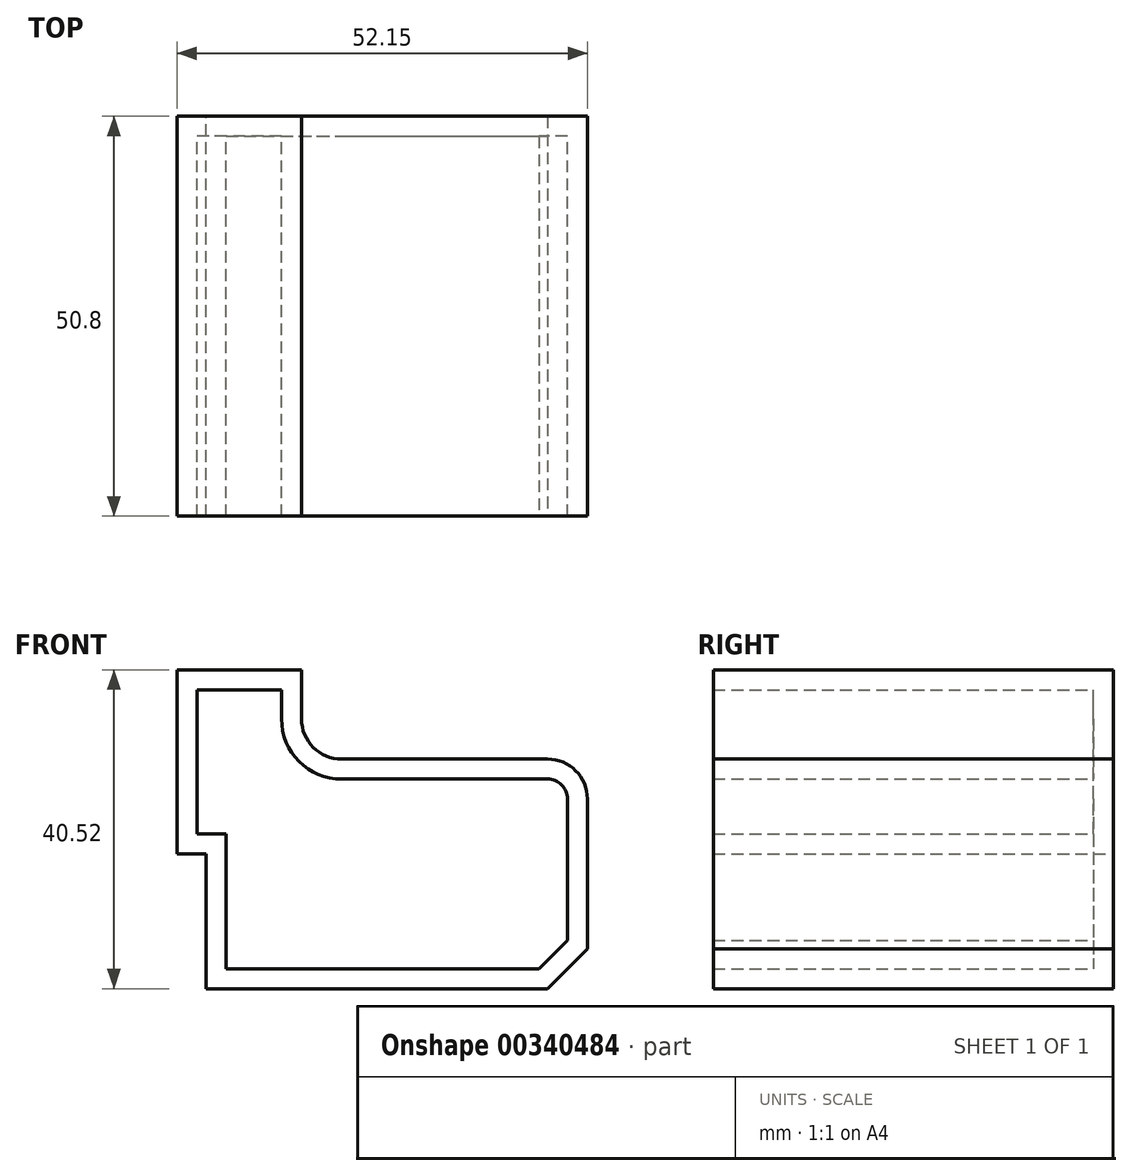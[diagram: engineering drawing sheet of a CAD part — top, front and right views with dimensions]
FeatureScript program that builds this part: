
annotation { "Feature Type Name" : "Feature", "Feature Type Description" : "" }
export const myFeature = defineFeature(function(context is Context, id is Id, definition is map)
    precondition{}
    {
        {
            var Q0;
            Q0=qCreatedBy(makeId("Front.planeOp"),FACE);
            var sketch = newSketch(context, id + "F0", { "sketchPlane" : qUnion([Q0])});
            skLineSegment(sketch, "E0.bottom", {"start": v(-97.79, 44.72) * mm, "end": v(-49.36, 44.72) * mm});
            skLineSegment(sketch, "E0.top", {"start": v(-97.79, 15.55) * mm, "end": v(-49.36, 15.55) * mm});
            skLineSegment(sketch, "E0.left", {"start": v(-97.79, 44.72) * mm, "end": v(-97.79, 15.55) * mm});
            skLineSegment(sketch, "E0.right", {"start": v(-49.36, 44.72) * mm, "end": v(-49.36, 15.55) * mm});
            skLineSegment(sketch, "E1.bottom", {"start": v(-85.68, 32.7) * mm, "end": v(-101.51, 32.7) * mm});
            skLineSegment(sketch, "E1.top", {"start": v(-85.68, 56.07) * mm, "end": v(-101.51, 56.07) * mm});
            skLineSegment(sketch, "E1.left", {"start": v(-85.68, 32.7) * mm, "end": v(-85.68, 56.07) * mm});
            skLineSegment(sketch, "E1.right", {"start": v(-101.51, 32.7) * mm, "end": v(-101.51, 56.07) * mm});
            skSolve(sketch);
        }
        {
            var Q0;
            {var subQ4=sQuery(id+"F0.wireOp",EDGE,"E1.top");Q0=makeQuery(id+"F0.imprint","IMPRINT",FACE,{"disambiguationData":[TD([[makeQuery(id+"F0.imprint","IMPRINT",EDGE,{"derivedFrom":subQ4}),1.0]])]});}
            var Q1;
            {var subQ0=sQuery(id+"F0.wireOp",EDGE,"E0.left");var subQ1=sQuery(id+"F0.wireOp",EDGE,"E0.bottom");var subQ2=makeQuery(id+"F0.imprint","INTERSECT",VERTEX,{"derivedFrom":[subQ1,subQ0]});Q1=makeQuery(id+"F0.imprint","IMPRINT",FACE,{"disambiguationData":[TD([[makeQuery(id+"F0.imprint","IMPRINT",EDGE,{"disambiguationData":[TD([[subQ2,-1.0]])],"derivedFrom":subQ1}),-1.0]])]});}
            var Q2;
            {var subQ2=sQuery(id+"F0.wireOp",EDGE,"E0.top");Q2=makeQuery(id+"F0.imprint","IMPRINT",FACE,{"disambiguationData":[TD([[makeQuery(id+"F0.imprint","IMPRINT",EDGE,{"derivedFrom":subQ2}),1.0]])]});}
            extrude(context, id + "F1", {"entities" : qUnion([Q0, Q1, Q2]), "depth" : 50.8 * mm});
        }
        {
            var Q0;
            Q0=makeQuery(id+"F1.opExtrude","SWEPT_EDGE",EDGE,{"disambiguationData":[OSD([sQuery(id+"F0.wireOp",EDGE,"E0.bottom"),sQuery(id+"F0.wireOp",EDGE,"E1.left")])]});
            var Q1;
            Q1=makeQuery(id+"F1.opExtrude","SWEPT_EDGE",EDGE,{"disambiguationData":[OSD([sQuery(id+"F0.wireOp",EDGE,"E0.bottom"),sQuery(id+"F0.wireOp",EDGE,"E0.right")])]});
            fillet(context, id + "F2", {"entities" : qUnion([Q0, Q1]), "radius" : 5.08 * mm, "tangentPropagation" : true, "allowEdgeOverflow" : false});
        }
        {
            var Q0;
            Q0=makeQuery(id+"F1.opExtrude","SWEPT_EDGE",EDGE,{"disambiguationData":[OSD([sQuery(id+"F0.wireOp",EDGE,"E0.top"),sQuery(id+"F0.wireOp",EDGE,"E0.right")])]});
            chamfer(context, id + "F3", {"entities" : qUnion([Q0]), "width" : 5.08 * mm, "tangentPropagation" : true});
        }
        {
            var Q0;
            Q0=makeQuery(id+"F1.opExtrude","CAP_FACE",FACE,{"disambiguationData":[OSD([sQuery(id+"F0.wireOp",EDGE,"E0.bottom"),sQuery(id+"F0.wireOp",EDGE,"E0.top"),sQuery(id+"F0.wireOp",EDGE,"E0.left"),sQuery(id+"F0.wireOp",EDGE,"E0.right"),sQuery(id+"F0.wireOp",EDGE,"E1.bottom"),sQuery(id+"F0.wireOp",EDGE,"E1.top"),sQuery(id+"F0.wireOp",EDGE,"E1.left"),sQuery(id+"F0.wireOp",EDGE,"E1.right")])],"isStart":false});
            shell(context, id + "F4", {"entities" : qUnion([Q0]), "thickness" : 2.54 * mm});
        }
    });
